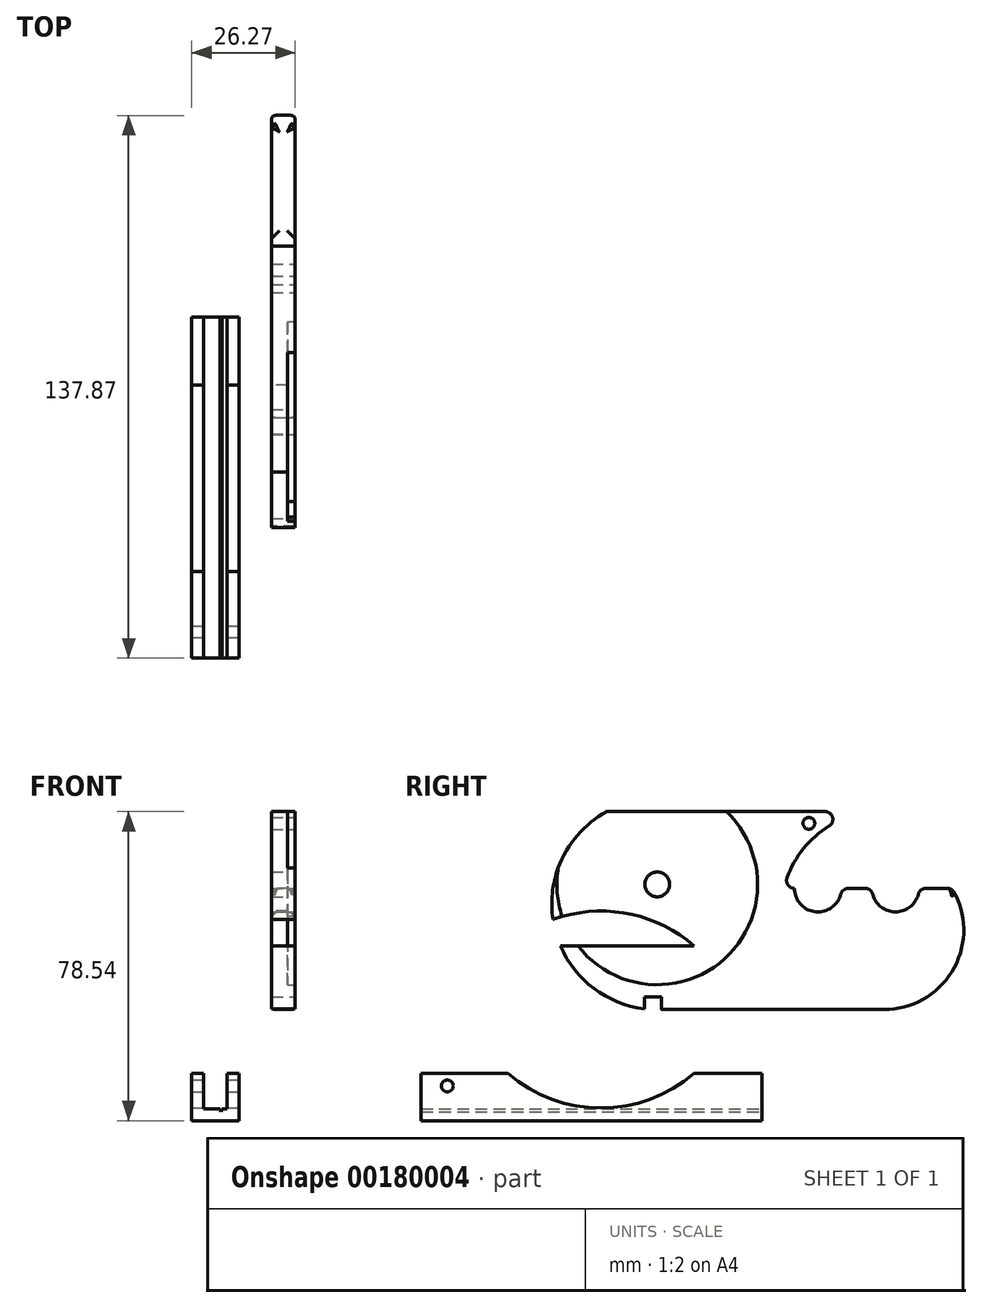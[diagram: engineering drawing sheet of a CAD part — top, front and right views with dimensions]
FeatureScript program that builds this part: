
annotation { "Feature Type Name" : "Feature", "Feature Type Description" : "" }
export const myFeature = defineFeature(function(context is Context, id is Id, definition is map)
    precondition{}
    {
        {
            assignVariable(context, id + "F0", {"name" : "Newsize", "anyValue" : 4.5});
        }
        {
            var Q0;
            Q0=qCreatedBy(makeId("Right.planeOp"),FACE);
            var sketch = newSketch(context, id + "F1", { "sketchPlane" : qUnion([Q0])});
            skCircle(sketch, "E0", {"center": v(0, 0) * mm, "radius": 22.5 * mm, "construction": true});
            skLineSegment(sketch, "E1", {"start": v(0, 0) * mm, "end": v(0, -22.5) * mm, "construction": true});
            skLineSegment(sketch, "E2", {"start": v(0, -22.5) * mm, "end": v(66.94, -22.5) * mm, "construction": true});
            skPoint(sketch, "E3", {"position": v(0, -18.5) * mm});
            skLineSegment(sketch, "E4", {"start": v(-20.54, -18.5) * mm, "end": v(42.62, -18.5) * mm});
            skLineSegment(sketch, "E5", {"start": v(34.86, 1.02) * mm, "end": v(74.86, 1.02) * mm});
            skLineSegment(sketch, "E6", {"start": v(57.68, 31.81) * mm, "end": v(1.1, 31.81) * mm});
            skArc(sketch, "E7", {"start": v(-3.25, 31.62) * mm, "mid": v(-26.31, 10.04) * mm, "end": v(-12.8, -18.5) * mm});
            skArc(sketch, "E8", {"start": v(32.98, -1.65) * mm, "mid": v(37.19, -9.14) * mm, "end": v(43.66, -14.8) * mm});
            skPoint(sketch, "E9.visualSharp", {"position": v(56.85, -18.5) * mm});
            skArc(sketch, "E9.filletArc", {"start": v(42.62, -18.5) * mm, "mid": v(44.54, -17.04) * mm, "end": v(43.66, -14.8) * mm});
            skPoint(sketch, "E10.visualSharp", {"position": v(32.2, 1.02) * mm});
            skArc(sketch, "E10.filletArc", {"start": v(34.86, 1.02) * mm, "mid": v(33.23, 0.18) * mm, "end": v(32.98, -1.65) * mm});
            skArc(sketch, "E11", {"start": v(74.86, 1.02) * mm, "mid": v(75.31, 21.46) * mm, "end": v(57.68, 31.81) * mm});
            skArc(sketch, "E12", {"start": v(46.82, 1.02) * mm, "mid": v(40.84, 7) * mm, "end": v(34.86, 1.02) * mm});
            skArc(sketch, "E13.1.0.0", {"start": v(66.52, 1.02) * mm, "mid": v(60.54, 7) * mm, "end": v(54.56, 1.02) * mm});
            skLineSegment(sketch, "E13.direction1", {"start": v(40.84, 1.02) * mm, "end": v(60.54, 1.02) * mm, "construction": true});
            skCircle(sketch, "E14", {"center": v(0, 0) * mm, "radius": 3.15 * mm});
            skCircle(sketch, "E15.0", {"center": v(0, 0) * mm, "radius": 25.5 * mm});
            skCircle(sketch, "E16", {"center": v(38.53, -15.5) * mm, "radius": 1.5 * mm});
            skLineSegment(sketch, "E17.top", {"start": v(1.1, 28.64) * mm, "end": v(-3.25, 28.64) * mm});
            skLineSegment(sketch, "E17.left", {"start": v(1.1, 31.81) * mm, "end": v(1.1, 28.64) * mm});
            skLineSegment(sketch, "E17.right", {"start": v(-3.25, 31.75) * mm, "end": v(-3.25, 28.64) * mm});
            skPoint(sketch, "E18.orphan", {"position": v(0, 31.81) * mm});
            skSolve(sketch);
        }
        {
            var Q0;
            Q0=makeQuery(id+"F1.imprint","IMPRINT",FACE,{"disambiguationData":[TD([[makeQuery(id+"F1.imprint","IMPRINT",EDGE,{"derivedFrom":sQuery(id+"F1.wireOp",EDGE,"E6")}),1.0]])]});
            var Q1;
            Q1=makeQuery(id+"F1.imprint","IMPRINT",FACE,{"disambiguationData":[TD([[makeQuery(id+"F1.imprint","IMPRINT",EDGE,{"derivedFrom":sQuery(id+"F1.wireOp",EDGE,"E14")}),-1.0]])]});
            var Q2;
            {var subQ1=sQuery(id+"F1.wireOp",EDGE,"E4");var subQ5=sQuery(id+"F1.wireOp",EDGE,"E15.0");var subQ7=makeQuery(id+"F1.imprint","INTERSECT",VERTEX,{"disambiguationData":[OD(1.0)],"derivedFrom":[subQ1,subQ5]});Q2=makeQuery(id+"F1.imprint","IMPRINT",FACE,{"disambiguationData":[TD([[makeQuery(id+"F1.imprint","IMPRINT",EDGE,{"disambiguationData":[TD([[subQ7,1.0]])],"derivedFrom":subQ1}),1.0]])]});}
            extrude(context, id + "F2", {"entities" : qUnion([Q0, Q1, Q2]), "depth" : 6 * mm});
        }
        {
            var Q0;
            Q0=makeQuery(id+"F1.imprint","IMPRINT",FACE,{"disambiguationData":[TD([[makeQuery(id+"F1.imprint","IMPRINT",EDGE,{"derivedFrom":sQuery(id+"F1.wireOp",EDGE,"E14")}),-1.0]])]});
            extrude(context, id + "F3", {"entities" : qUnion([Q0]), "operationType" : NewBodyOperationType.REMOVE, "depth" : (6.4 - getVariable(context, 'Newsize')) * mm});
        }
        {
            var Q0;
            Q0=makeQuery(id+"F2.opExtrude","SWEPT_FACE",FACE,{"disambiguationData":[OSD([sQuery(id+"F1.wireOp",EDGE,"E13.3.0.0")])]});
            var Q1;
            Q1=makeQuery(id+"F2.opExtrude","SWEPT_FACE",FACE,{"disambiguationData":[OSD([sQuery(id+"F1.wireOp",EDGE,"E13.2.0.0")])]});
            var Q2;
            Q2=makeQuery(id+"F2.opExtrude","SWEPT_FACE",FACE,{"disambiguationData":[OSD([sQuery(id+"F1.wireOp",EDGE,"E13.1.0.0")])]});
            var Q3;
            {var subQ0=sQuery(id+"F1.wireOp",EDGE,"E5");Q3=makeQuery(id+"F2.opExtrude","SWEPT_FACE",FACE,{"disambiguationData":[OSD([subQ0]),TDD([makeQuery(id+"F1.imprint","IMPRINT",EDGE,{"disambiguationData":[TD([[makeQuery(id+"F1.imprint","INTERSECT",VERTEX,{"disambiguationData":[OD(0.0)],"derivedFrom":[subQ0,sQuery(id+"F1.wireOp",EDGE,"E13.2.0.0")]}),-1.0]])],"derivedFrom":subQ0})])]});}
            var Q4;
            {var subQ0=sQuery(id+"F1.wireOp",EDGE,"E5");Q4=makeQuery(id+"F2.opExtrude","SWEPT_FACE",FACE,{"disambiguationData":[OSD([subQ0]),TDD([makeQuery(id+"F1.imprint","IMPRINT",EDGE,{"disambiguationData":[TD([[makeQuery(id+"F1.imprint","INTERSECT",VERTEX,{"disambiguationData":[OD(0.0)],"derivedFrom":[subQ0,sQuery(id+"F1.wireOp",EDGE,"E13.1.0.0")]}),-1.0]])],"derivedFrom":subQ0})])]});}
            var Q5;
            {var subQ0=sQuery(id+"F1.wireOp",EDGE,"E5");Q5=makeQuery(id+"F2.opExtrude","SWEPT_FACE",FACE,{"disambiguationData":[OSD([subQ0]),TDD([makeQuery(id+"F1.imprint","IMPRINT",EDGE,{"disambiguationData":[TD([[makeQuery(id+"F1.imprint","INTERSECT",VERTEX,{"derivedFrom":[subQ0,sQuery(id+"F1.wireOp",EDGE,"E11")]}),1.0]])],"derivedFrom":subQ0})])]});}
            var Q6;
            {var subQ0=sQuery(id+"F1.wireOp",EDGE,"E5");Q6=makeQuery(id+"F2.opExtrude","SWEPT_FACE",FACE,{"disambiguationData":[OSD([subQ0]),TDD([makeQuery(id+"F1.imprint","IMPRINT",EDGE,{"disambiguationData":[TD([[makeQuery(id+"F1.imprint","INTERSECT",VERTEX,{"derivedFrom":[subQ0,sQuery(id+"F1.wireOp",EDGE,"E12")]}),-1.0]])],"derivedFrom":subQ0})])]});}
            fillet(context, id + "F4", {"entities" : qUnion([Q0, Q1, Q2, Q3, Q4, Q5, Q6]), "radius" : 2 * mm, "tangentPropagation" : true, "allowEdgeOverflow" : false});
        }
        {
            var Q0;
            Q0=makeQuery(id+"F2.opExtrude","SWEPT_FACE",FACE,{"disambiguationData":[OSD([sQuery(id+"F1.wireOp",EDGE,"E11")])]});
            fillet(context, id + "F5", {"entities" : qUnion([Q0]), "radius" : 1 * mm, "tangentPropagation" : true, "allowEdgeOverflow" : false});
        }
        {
            var Q0;
            Q0=qCreatedBy(makeId("Front.planeOp"),FACE);
            var sketch = newSketch(context, id + "F6", { "sketchPlane" : qUnion([Q0])});
            skLineSegment(sketch, "E19.bottom", {"start": v(-7.27, 6.6) * mm, "end": v(-8.52, 6.6) * mm});
            skLineSegment(sketch, "E19.left", {"start": v(-7.27, 6.6) * mm, "end": v(-7.27, 15.6) * mm});
            skLineSegment(sketch, "E19.right", {"start": v(-13.27, 6.6) * mm, "end": v(-13.27, 15.6) * mm});
            skPoint(sketch, "E19.middle", {"position": v(-10.27, 11.1) * mm});
            skLineSegment(sketch, "E20.0", {"start": v(-16.27, 3.6) * mm, "end": v(-16.27, 15.6) * mm});
            skLineSegment(sketch, "E20.1", {"start": v(-4.27, 3.6) * mm, "end": v(-16.27, 3.6) * mm});
            skLineSegment(sketch, "E20.2", {"start": v(-4.27, 3.6) * mm, "end": v(-4.27, 15.6) * mm});
            skLineSegment(sketch, "E21", {"start": v(-16.27, 15.6) * mm, "end": v(-13.27, 15.6) * mm});
            skLineSegment(sketch, "E22", {"start": v(-7.27, 15.6) * mm, "end": v(-4.27, 15.6) * mm});
            skLineSegment(sketch, "E23", {"start": v(-8.52, 6.6) * mm, "end": v(-8.77, 5.77) * mm});
            skLineSegment(sketch, "E24", {"start": v(-8.77, 5.77) * mm, "end": v(-9.02, 6.6) * mm});
            skLineSegment(sketch, "E25.trimOffspring", {"start": v(-9.02, 6.6) * mm, "end": v(-13.27, 6.6) * mm});
            skSolve(sketch);
        }
        {
            var Q0;
            Q0=makeQuery(id+"F6.imprint","IMPRINT",FACE,{"disambiguationData":[TD([[makeQuery(id+"F6.imprint","IMPRINT",EDGE,{"derivedFrom":sQuery(id+"F6.wireOp",EDGE,"E19.bottom")}),1.0]])]});
            extrude(context, id + "F7", {"entities" : qUnion([Q0]), "depth" : 60 * mm, "hasSecondDirection" : true, "secondDirectionOppositeDirection" : true, "secondDirectionDepth" : 26.6 * mm});
        }
        {
            var Q0;
            Q0=makeQuery(id+"F7.opExtrude","SWEPT_FACE",FACE,{"disambiguationData":[OSD([sQuery(id+"F6.wireOp",EDGE,"E19.right")])]});
            var sketch = newSketch(context, id + "F8", { "sketchPlane" : qUnion([Q0])});
            skLineSegment(sketch, "E26", {"start": v(-53.32, 6.42) * mm, "end": v(-53.32, 10.42) * mm});
            skCircle(sketch, "E27", {"center": v(-53.32, 12.42) * mm, "radius": 1.5 * mm});
            skArc(sketch, "E28", {"start": v(-37.97, 15.6) * mm, "mid": v(-14.3, 6.79) * mm, "end": v(9.37, 15.6) * mm});
            skSolve(sketch);
        }
        {
            var Q0;
            Q0=makeQuery(id+"F8.imprint","IMPRINT",FACE,{"disambiguationData":[TD([[makeQuery(id+"F8.imprint","IMPRINT",EDGE,{"derivedFrom":sQuery(id+"F8.wireOp",EDGE,"E27")}),1.0]])]});
            var Q1;
            {var subQ0=sQuery(id+"F8.wireOp",EDGE,"E28");Q1=makeQuery(id+"F8.imprint","IMPRINT",FACE,{"disambiguationData":[TD([[makeQuery(id+"F8.imprint","IMPRINT",EDGE,{"derivedFrom":subQ0}),1.0]])]});}
            extrude(context, id + "F9", {"entities" : qUnion([Q0, Q1]), "operationType" : NewBodyOperationType.REMOVE, "oppositeDirection" : true, "depth" : 25 * mm, "hasSecondDirection" : true, "secondDirectionOppositeDirection" : false, "secondDirectionDepth" : 25 * mm});
        }
        {
            var Q0;
            Q0=makeQuery(id+"F2.opExtrude","SWEPT_BODY",BODY,{"disambiguationData":[OSD([sQuery(id+"F1.wireOp",EDGE,"E4"),sQuery(id+"F1.wireOp",EDGE,"E5"),sQuery(id+"F1.wireOp",EDGE,"E6"),sQuery(id+"F1.wireOp",EDGE,"E7"),sQuery(id+"F1.wireOp",EDGE,"E8"),sQuery(id+"F1.wireOp",EDGE,"E9.filletArc"),sQuery(id+"F1.wireOp",EDGE,"E10.filletArc"),sQuery(id+"F1.wireOp",EDGE,"E11"),sQuery(id+"F1.wireOp",EDGE,"E12"),sQuery(id+"F1.wireOp",EDGE,"E13.1.0.0"),sQuery(id+"F1.wireOp",EDGE,"E13.2.0.0"),sQuery(id+"F1.wireOp",EDGE,"E14"),sQuery(id+"F1.wireOp",EDGE,"E16"),sQuery(id+"F1.wireOp",EDGE,"E17.top"),sQuery(id+"F1.wireOp",EDGE,"E17.left"),sQuery(id+"F1.wireOp",EDGE,"E17.right")])]});
            var Q1;
            {var subQ0=sQuery(id+"F1.wireOp",EDGE,"E6");Q1=makeQuery(id+"F5.opFillet","BLEND_EDGE",EDGE,{"blendedFrom":[makeQuery(id+"F2.opExtrude","CAP_EDGE",EDGE,{"disambiguationData":[OSD([subQ0])],"isStart":false}),makeQuery(id+"F2.opExtrude","SWEPT_FACE",FACE,{"disambiguationData":[OSD([subQ0])]})],"blendedInto":[makeQuery(id+"F2.opExtrude","SWEPT_FACE",FACE,{"disambiguationData":[OSD([subQ0])]})]});}
            transform(context, id + "F10", {"entities" : qUnion([Q0]), "transformType" : TransformType.ROTATION, "transformAxis" : qUnion([Q1]), "angle" : 180 * degree, "makeCopy" : false});
        }
    });
